# Revit family: Ventüer_VentilationLouvres_VL-100S
name_source: partatom
category: Generic Models
units: mm (PartAtom-declared; Revit-internal decimal feet)

## family parameters
Always vertical = No
Can host rebar = No
Cut with Voids When Loaded = Yes
Part Type = Normal
Room Calculation Point = No
Round Connector Dimension = Use Diameter
Shared = No
Work Plane-Based = Yes

## types (5) — shared parameters
Aerodynamic Performance = Air Inlet: 0.313, Class 2. Air Extract: 0.304, Class 2
Ancillaries = Bird Mesh, Insect Mesh, Solid Blanking, Perimeter Mounting Angle
Blade Centres = 100 mm  [stored 0.328084 ft]
Blade Material = Ventüer Aluminium
Default Elevation = 1219 mm
Description = Maximum Airflow for Exhaust
Exact Neck Height = 594 mm
Exact Neck Height Check = 594 mm
Exact Neck Width = 594 mm
Exact Neck Width Check = 594 mm
Frame Material = Ventüer Aluminium
Frame Set Count = 1
Frame Set Count Check = 2
Frame Set Transition Count = 1
Frame Set Transition Count Check = 2
Manufacturer = Ventüer
Max Flow = 5000.0 L/s
Min Flow = 100.0 L/s
Model = VL-100S
Multiple Frame Set = No
Multiple Transition = No
Noise Level NC Max = 0.00 NC
Noise Level NC Min = 0.00 NC
Nominal Height = 600 mm
Nominal Width = 600 mm
Nominated Air Flow = 100.0 L/s
Nominated Pessure Drop = 21.0 Pa
Rain Defence Performance = Class B - up to 0.5m/s suction velocity. Class C - up to 2.5m/s suction velocity. Class D - up to 3.5m/s suction velocity
SHS = No
Single Frame Set = Yes
Single Transition = No
Specified Air Flow = 0.0 L/s
Specified Pressure Drop = 21.0 Pa
Static Pressure Max = 60.0 Pa
Static Pressure Min = 10.0 Pa
URL = https://www.ventuer.co
Ventüer Product Range = Ventilation Louvres

## per-type parameters (varying)
- VL-100S_CF: Base Width=3 mm  [stored 0.00984252 ft]; Blade And Frame Gap=32 mm  [stored 0.104987 ft]; Blade Count=5; Blade Cut Offset=500 mm  [stored 1.64042 ft]; Blade Horizontal Offset=3 mm  [stored 0.00984252 ft]; Channel=Yes; Clip=No; Clip Frame Height=548 mm; Connector Height=583 mm; Connector Width=583 mm; Depth=100 mm  [stored 0.328084 ft]; Flanged 1=No; Flanged 2=No; Frame Set Width=579 mm; Glazed=No; Overall Opening Height=583 mm; Overall Opening Width=583 mm; Profile Width=8 mm  [stored 0.0262467 ft]; Screen Symbol Distance=3 mm  [stored 0.00984252 ft]; Siffener Length=588 mm; Single Frame Set Width=289 mm; Support To Frame Gap=44 mm  [stored 0.144357 ft]; Tee=Yes; Top Blade=Yes; Top Blade Corrector=5 mm  [stored 0.0164042 ft]; Top Blade Height=56 mm
- VL-100S_GF: Base Width=26 mm; Blade And Frame Gap=10 mm  [stored 0.0328084 ft]; Blade Count=5; Blade Cut Offset=500 mm  [stored 1.64042 ft]; Blade Horizontal Offset=8 mm  [stored 0.0262467 ft]; Channel=No; Clip=No; Clip Frame Height=526 mm; Connector Height=532 mm; Connector Width=532 mm; Depth=105 mm  [stored 0.344488 ft]; Flanged 1=No; Flanged 2=No; Frame Set Width=521 mm; Glazed=Yes; Overall Opening Height=532 mm; Overall Opening Width=532 mm; Profile Width=37 mm; Screen Symbol Distance=6 mm  [stored 0.019685 ft]; Siffener Length=542 mm; Single Frame Set Width=261 mm; Support To Frame Gap=22 mm  [stored 0.0721785 ft]; Tee=Yes; Top Blade=Yes; Top Blade Corrector=11 mm; Top Blade Height=32 mm  [stored 0.104987 ft]
- VL-100S_FF_1: Base Width=52 mm; Blade And Frame Gap=10 mm  [stored 0.0328084 ft]; Blade Count=4; Blade Cut Offset=400 mm  [stored 1.31234 ft]; Blade Horizontal Offset=5 mm  [stored 0.0164042 ft]; Channel=No; Clip=No; Clip Frame Height=426 mm; Connector Height=490 mm  [stored 1.60761 ft]; Connector Width=490 mm  [stored 1.60761 ft]; Depth=101 mm; Flanged 1=Yes; Flanged 2=No; Frame Set Width=490 mm  [stored 1.60761 ft]; Glazed=No; Overall Opening Height=490 mm  [stored 1.60761 ft]; Overall Opening Width=490 mm  [stored 1.60761 ft]; Profile Width=52 mm; Screen Symbol Distance=4 mm  [stored 0.0131234 ft]; Siffener Length=490 mm  [stored 1.60761 ft]; Single Frame Set Width=245 mm  [stored 0.803806 ft]; Support To Frame Gap=22 mm  [stored 0.0721785 ft]; Tee=Yes; Top Blade=Yes; Top Blade Corrector=0 mm  [stored 0 ft]; Top Blade Height=80 mm
- VL-100S_FF_2: Base Width=24 mm  [stored 0.0787402 ft]; Blade And Frame Gap=10 mm  [stored 0.0328084 ft]; Blade Count=5; Blade Cut Offset=500 mm  [stored 1.64042 ft]; Blade Horizontal Offset=3 mm  [stored 0.00984252 ft]; Channel=No; Clip=No; Clip Frame Height=526 mm; Connector Height=546 mm; Connector Width=546 mm; Depth=100 mm  [stored 0.328084 ft]; Flanged 1=No; Flanged 2=Yes; Frame Set Width=546 mm; Glazed=No; Overall Opening Height=546 mm; Overall Opening Width=546 mm; Profile Width=24 mm  [stored 0.0787402 ft]; Screen Symbol Distance=3 mm  [stored 0.00984252 ft]; Siffener Length=546 mm; Single Frame Set Width=273 mm; Support To Frame Gap=22 mm  [stored 0.0721785 ft]; Tee=Yes; Top Blade=Yes; Top Blade Corrector=0 mm  [stored 0 ft]; Top Blade Height=36 mm
- VL-100S_Clip: Base Width=0 mm  [stored 0 ft]; Blade And Frame Gap=32 mm  [stored 0.104987 ft]; Blade Count=5; Blade Cut Offset=500 mm  [stored 1.64042 ft]; Blade Horizontal Offset=3 mm  [stored 0.00984252 ft]; Channel=No; Clip=Yes; Clip Frame Height=548 mm; Connector Height=594 mm; Connector Width=594 mm; Depth=99 mm; Flanged 1=No; Flanged 2=No; Frame Set Width=594 mm; Glazed=No; Overall Opening Height=594 mm; Overall Opening Width=594 mm; Profile Width=0 mm  [stored 0 ft]; Screen Symbol Distance=3 mm  [stored 0.00984252 ft]; Siffener Length=599 mm; Single Frame Set Width=297 mm  [stored 0.974409 ft]; Support To Frame Gap=44 mm  [stored 0.144357 ft]; Tee=No; Top Blade=No; Top Blade Corrector=5 mm  [stored 0.0164042 ft]; Top Blade Height=67 mm

note: column(s) folded — value = type name in every type: Keynote

note: [stored X ft] marks values corroborated as IEEE doubles in the binary element streams (Revit-internal decimal feet)

## geometry (parser evidence)
native form markers: Sweep x16
no freeform markers — native parametric forms only
